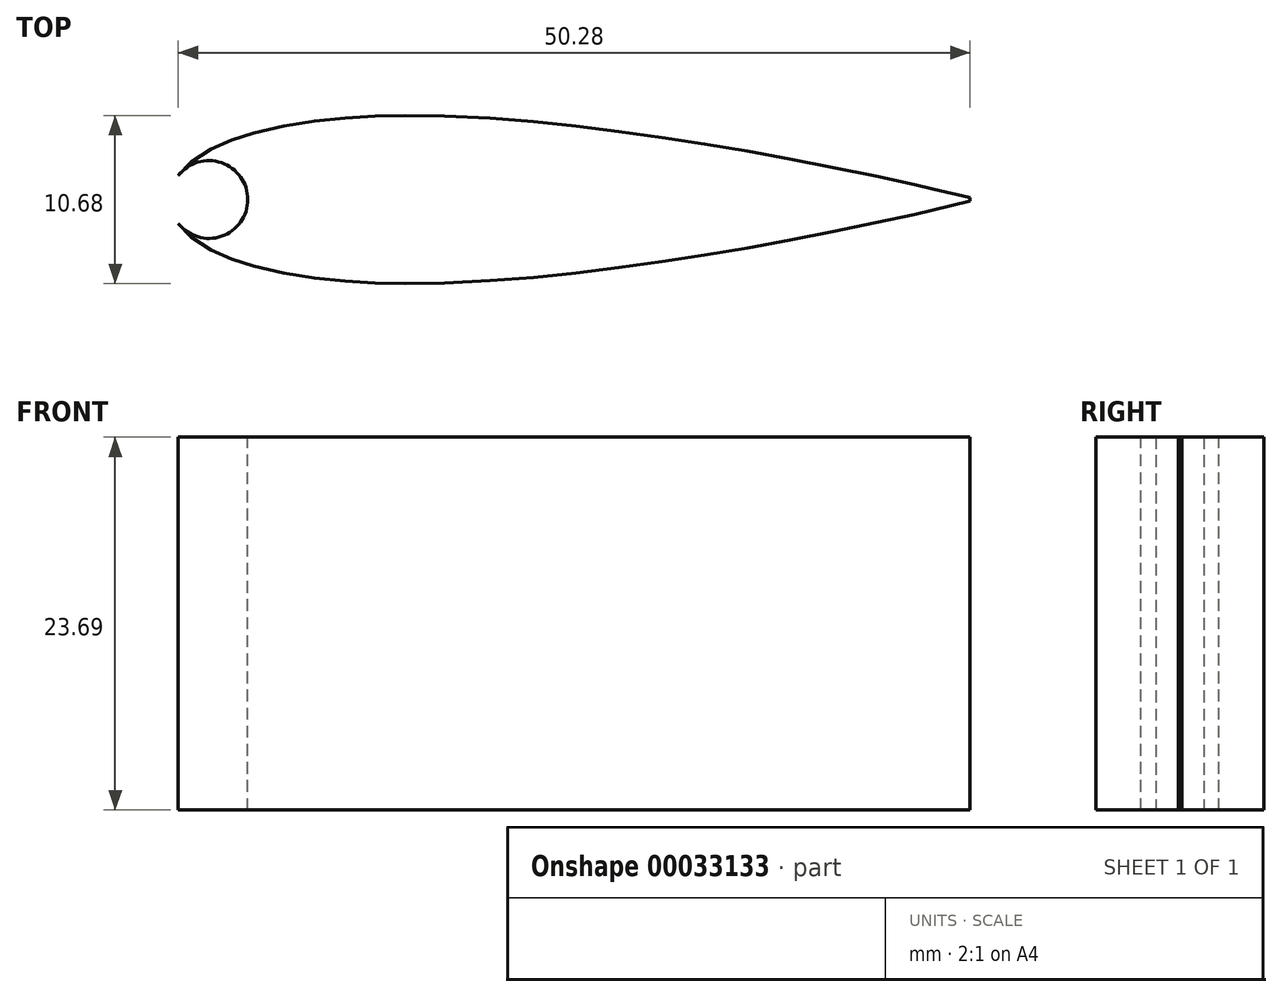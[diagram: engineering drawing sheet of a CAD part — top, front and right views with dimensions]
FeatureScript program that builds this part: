
annotation { "Feature Type Name" : "Feature", "Feature Type Description" : "" }
export const myFeature = defineFeature(function(context is Context, id is Id, definition is map)
    precondition{}
    {
        {
            var Q0;
            Q0=qCreatedBy(makeId("Top.planeOp"),FACE);
            var sketch = newSketch(context, id + "F0", { "sketchPlane" : qUnion([Q0])});
            skFitSpline(sketch, "E0", {"points": [v(50.8, 0.11) * mm, v(48.26, 0.72) * mm, v(45.72, 1.29) * mm, v(40.64, 2.33) * mm, v(35.56, 3.26) * mm, v(30.48, 4.06) * mm, v(25.4, 4.7) * mm, v(20.32, 5.16) * mm, v(15.24, 5.34) * mm, v(12.7, 5.28) * mm, v(10.16, 5.1) * mm, v(7.62, 4.75) * mm, v(5.08, 4.16) * mm, v(3.81, 3.73) * mm, v(2.54, 3.16) * mm, v(1.27, 2.32) * mm, v(0.64, 1.68) * mm, v(0, 0) * mm, v(0.64, -1.68) * mm, v(1.27, -2.32) * mm, v(2.54, -3.16) * mm, v(3.81, -3.73) * mm, v(5.08, -4.16) * mm, v(7.62, -4.75) * mm, v(10.16, -5.1) * mm, v(12.7, -5.28) * mm, v(15.24, -5.34) * mm, v(20.32, -5.16) * mm, v(25.4, -4.7) * mm, v(30.48, -4.06) * mm, v(35.56, -3.26) * mm, v(40.64, -2.33) * mm, v(45.72, -1.29) * mm, v(48.26, -0.72) * mm, v(50.8, -0.11) * mm], "startDerivative": vector(-274.37, 65.35) * mm, "endDerivative": vector(274.37, 65.35) * mm});
            skPoint(sketch, "E1", {"position": v(160.75, -18.69) * mm});
            skLineSegment(sketch, "E2", {"start": v(50.8, 0.11) * mm, "end": v(50.8, -0.11) * mm});
            skCircle(sketch, "E3", {"center": v(2.47, 0) * mm, "radius": 2.47 * mm, "construction": true});
            skSolve(sketch);
        }
        {
            var Q0;
            Q0 = qSketchRegion(id + "F0", true);
            extrude(context, id + "F1", {"entities" : qUnion([Q0]), "depth" : (24 - (0.12 * 2.5)) * mm});
        }
        {
            var Q0;
            Q0=makeQuery(id+"F1.opExtrude","CAP_FACE",FACE,{"disambiguationData":[OSD([sQuery(id+"F0.wireOp",EDGE,"E0"),sQuery(id+"F0.wireOp",EDGE,"E2")])],"isStart":false});
            var sketch = newSketch(context, id + "F2", { "sketchPlane" : qUnion([Q0])});
            skCircle(sketch, "E4", {"center": v(2.47, 0) * mm, "radius": 2.47 * mm});
            skSolve(sketch);
        }
        {
            var Q0;
            Q0 = qSketchRegion(id + "F2", true);
            extrude(context, id + "F3", {"entities" : qUnion([Q0]), "operationType" : NewBodyOperationType.REMOVE, "endBound" : BoundingType.THROUGH_ALL, "oppositeDirection" : true, "depth" : 25.4 * mm});
        }
    });
